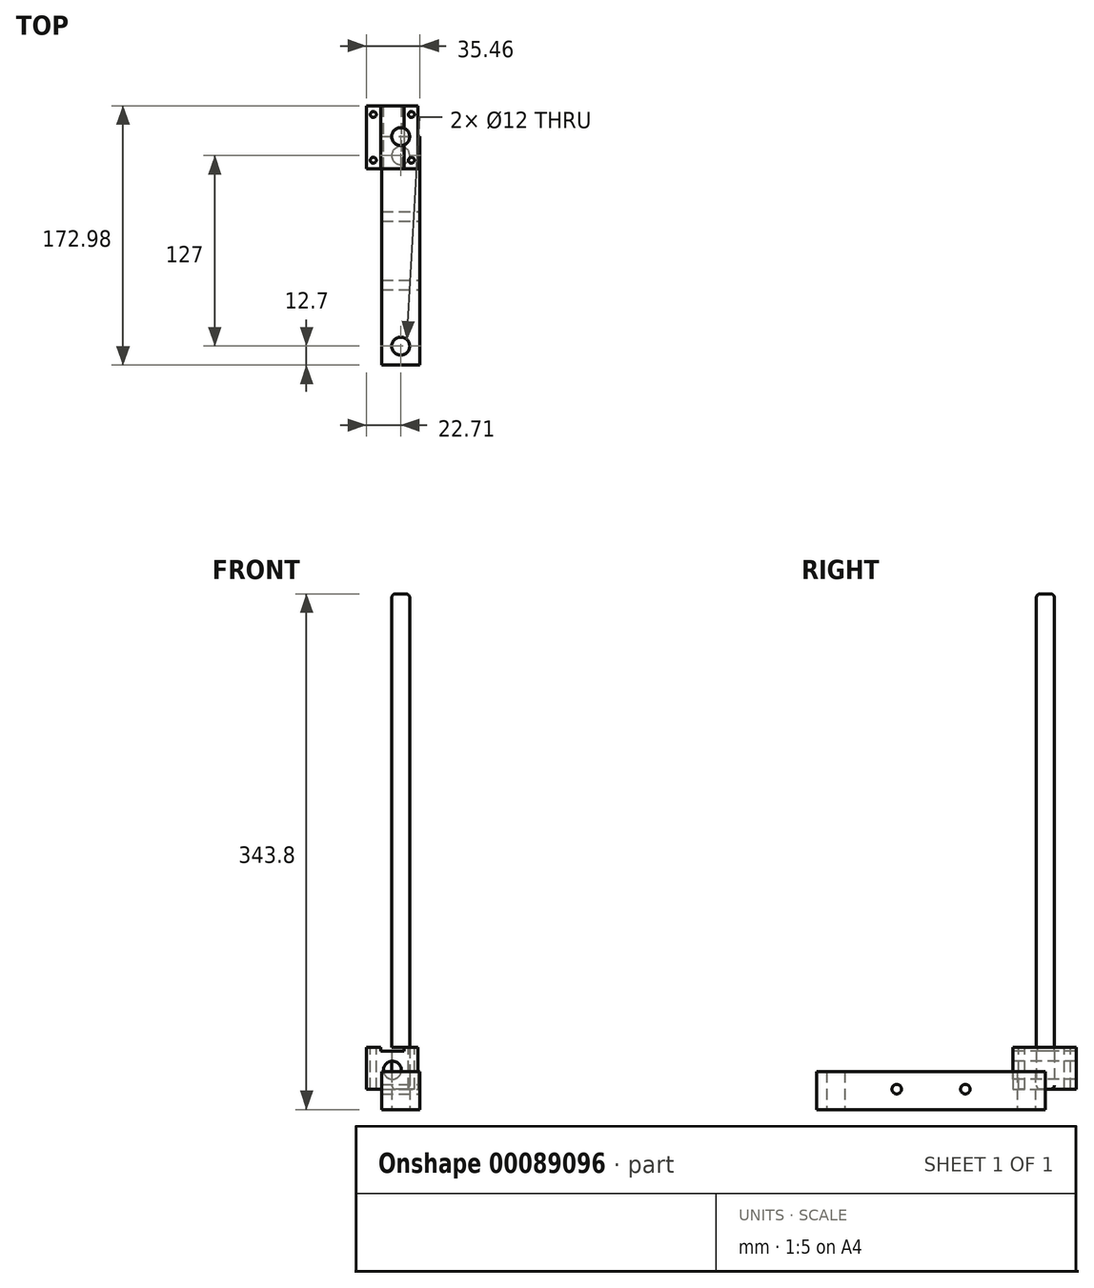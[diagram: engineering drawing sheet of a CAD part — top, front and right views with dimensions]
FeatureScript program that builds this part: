
annotation { "Feature Type Name" : "Feature", "Feature Type Description" : "" }
export const myFeature = defineFeature(function(context is Context, id is Id, definition is map)
    precondition{}
    {
        {
            var Q0;
            Q0=qCreatedBy(makeId("Top.planeOp"),FACE);
            var sketch = newSketch(context, id + "F0", { "sketchPlane" : qUnion([Q0])});
            skCircle(sketch, "E0", {"center": v(0, 0) * mm, "radius": 6 * mm});
            skSolve(sketch);
        }
        {
            var Q0;
            Q0 = qSketchRegion(id + "F0", true);
            extrude(context, id + "F1", {"entities" : qUnion([Q0]), "depth" : 330.2 * mm});
        }
        {
            var Q0;
            Q0=makeQuery(id+"F1.opExtrude","CAP_EDGE",EDGE,{"disambiguationData":[OSD([sQuery(id+"F0.wireOp",EDGE,"E0")])],"isStart":false});
            var Q1;
            Q1=makeQuery(id+"F1.opExtrude","CAP_EDGE",EDGE,{"disambiguationData":[OSD([sQuery(id+"F0.wireOp",EDGE,"E0")])],"isStart":true});
            fillet(context, id + "F2", {"entities" : qUnion([Q0, Q1]), "radius" : 2.54 * mm, "tangentPropagation" : true, "allowEdgeOverflow" : false});
        }
        {
            var Q0;
            Q0=qCreatedBy(makeId("Front.planeOp"),FACE);
            var sketch = newSketch(context, id + "F3", { "sketchPlane" : qUnion([Q0])});
            skLineSegment(sketch, "E1.bottom", {"start": v(-12.65, -13.6) * mm, "end": v(12.75, -13.6) * mm});
            skLineSegment(sketch, "E1.top", {"start": v(-12.65, 11.8) * mm, "end": v(12.75, 11.8) * mm});
            skLineSegment(sketch, "E1.left", {"start": v(-12.65, -13.6) * mm, "end": v(-12.65, 11.8) * mm});
            skLineSegment(sketch, "E1.right", {"start": v(12.75, -13.6) * mm, "end": v(12.75, 11.8) * mm});
            skSolve(sketch);
        }
        {
            var Q0;
            Q0 = qSketchRegion(id + "F3", true);
            extrude(context, id + "F4", {"entities" : qUnion([Q0]), "depth" : 152.4 * mm});
        }
        {
            var Q0;
            Q0=makeQuery(id+"F4.opExtrude","SWEPT_FACE",FACE,{"disambiguationData":[OSD([sQuery(id+"F3.wireOp",EDGE,"E1.bottom")])]});
            var sketch = newSketch(context, id + "F5", { "sketchPlane" : qUnion([Q0])});
            skPoint(sketch, "E2", {"position": v(0, 12.7) * mm});
            skPoint(sketch, "E3", {"position": v(0, 139.7) * mm});
            skSolve(sketch);
        }
        {
            var Q0;
            Q0=sQuery(id+"F5.wireOp",VERTEX,"E3");
            var Q1;
            Q1=sQuery(id+"F5.wireOp",VERTEX,"E2");
            var Q2;
            Q2=makeQuery(id+"F4.opExtrude","SWEPT_BODY",BODY,{"disambiguationData":[OSD([sQuery(id+"F3.wireOp",EDGE,"E1.bottom"),sQuery(id+"F3.wireOp",EDGE,"E1.top"),sQuery(id+"F3.wireOp",EDGE,"E1.left"),sQuery(id+"F3.wireOp",EDGE,"E1.right")])]});
            hole(context, id + "F6", {"style" : HoleStyle.SIMPLE, "endStyle" : HoleEndStyle.THROUGH, "holeDiameter" : 12 * mm, "locations" : qUnion([Q0, Q1]), "scope" : qUnion([Q2]), "isTappedThrough" : true});
        }
        {
            var Q0;
            Q0=makeQuery(id+"F4.opExtrude","SWEPT_FACE",FACE,{"disambiguationData":[OSD([sQuery(id+"F3.wireOp",EDGE,"E1.right")])]});
            var sketch = newSketch(context, id + "F7", { "sketchPlane" : qUnion([Q0])});
            skPoint(sketch, "E4", {"position": v(-53.34, 0) * mm});
            skPoint(sketch, "E5", {"position": v(-99.06, 0) * mm});
            skSolve(sketch);
        }
        {
            var Q0;
            Q0=sQuery(id+"F7.wireOp",VERTEX,"E5");
            var Q1;
            Q1=sQuery(id+"F7.wireOp",VERTEX,"E4");
            var Q2;
            Q2=makeQuery(id+"F4.opExtrude","SWEPT_BODY",BODY,{"disambiguationData":[OSD([sQuery(id+"F3.wireOp",EDGE,"E1.bottom"),sQuery(id+"F3.wireOp",EDGE,"E1.top"),sQuery(id+"F3.wireOp",EDGE,"E1.left"),sQuery(id+"F3.wireOp",EDGE,"E1.right")])]});
            hole(context, id + "F8", {"style" : HoleStyle.SIMPLE, "endStyle" : HoleEndStyle.THROUGH, "holeDiameter" : 6.35 * mm, "locations" : qUnion([Q0, Q1]), "scope" : qUnion([Q2]), "isTappedThrough" : true});
        }
        {
            var Q0;
            Q0=qCreatedBy(makeId("Top.planeOp"),FACE);
            var sketch = newSketch(context, id + "F9", { "sketchPlane" : qUnion([Q0])});
            skLineSegment(sketch, "E6.bottom", {"start": v(-22.71, -21.58) * mm, "end": v(11.58, -21.58) * mm});
            skLineSegment(sketch, "E6.top", {"start": v(-22.71, 20.58) * mm, "end": v(11.58, 20.58) * mm});
            skLineSegment(sketch, "E6.left", {"start": v(-22.71, -21.58) * mm, "end": v(-22.71, 20.58) * mm});
            skLineSegment(sketch, "E6.right", {"start": v(11.58, -21.58) * mm, "end": v(11.58, 20.58) * mm});
            skSolve(sketch);
        }
        {
            var Q0;
            Q0=makeQuery(id+"F9.imprint","IMPRINT",FACE,{"disambiguationData":[TD([[makeQuery(id+"F9.imprint","IMPRINT",EDGE,{"derivedFrom":sQuery(id+"F9.wireOp",EDGE,"E6.bottom")}),1.0]])]});
            extrude(context, id + "F10", {"entities" : qUnion([Q0]), "depth" : 27.94 * mm});
        }
        {
            var Q0;
            Q0=makeQuery(id+"F10.opExtrude","CAP_FACE",FACE,{"disambiguationData":[OSD([sQuery(id+"F9.wireOp",EDGE,"E6.bottom"),sQuery(id+"F9.wireOp",EDGE,"E6.top"),sQuery(id+"F9.wireOp",EDGE,"E6.left"),sQuery(id+"F9.wireOp",EDGE,"E6.right")])],"isStart":false});
            var sketch = newSketch(context, id + "F11", { "sketchPlane" : qUnion([Q0])});
            skPoint(sketch, "E7", {"position": v(-18.27, -15.74) * mm});
            skPoint(sketch, "E8", {"position": v(-18.27, 14.74) * mm});
            skLineSegment(sketch, "E9", {"start": v(-5.57, 20.58) * mm, "end": v(-5.57, -21.58) * mm});
            skPoint(sketch, "E10.MirrorP", {"position": v(7.13, 14.74) * mm});
            skPoint(sketch, "E11.MirrorP", {"position": v(7.13, -15.74) * mm});
            skSolve(sketch);
        }
        {
            var Q0;
            Q0=sQuery(id+"F11.wireOp",VERTEX,"E8");
            var Q1;
            Q1=sQuery(id+"F11.wireOp",VERTEX,"E7");
            var Q2;
            Q2=sQuery(id+"F11.wireOp",VERTEX,"E11.MirrorP");
            var Q3;
            Q3=sQuery(id+"F11.wireOp",VERTEX,"E10.MirrorP");
            var Q4;
            Q4=makeQuery(id+"F10.opExtrude","SWEPT_BODY",BODY,{"disambiguationData":[OSD([sQuery(id+"F9.wireOp",EDGE,"E6.bottom"),sQuery(id+"F9.wireOp",EDGE,"E6.top"),sQuery(id+"F9.wireOp",EDGE,"E6.left"),sQuery(id+"F9.wireOp",EDGE,"E6.right")])]});
            hole(context, id + "F12", {"style" : HoleStyle.SIMPLE, "endStyle" : HoleEndStyle.THROUGH, "holeDiameter" : 4 * mm, "locations" : qUnion([Q0, Q1, Q2, Q3]), "scope" : qUnion([Q4]), "isTappedThrough" : true});
        }
        {
            var Q0;
            Q0=makeQuery(id+"F10.opExtrude","SWEPT_FACE",FACE,{"disambiguationData":[OSD([sQuery(id+"F9.wireOp",EDGE,"E6.bottom")])]});
            var sketch = newSketch(context, id + "F13", { "sketchPlane" : qUnion([Q0])});
            skPoint(sketch, "E12", {"position": v(-5.57, 13.97) * mm});
            skPoint(sketch, "E13", {"position": v(-5.57, 12.6) * mm});
            skLineSegment(sketch, "E14.bottom", {"start": v(-5.57, 27.94) * mm, "end": v(-13.43, 27.94) * mm});
            skLineSegment(sketch, "E14.top", {"start": v(-5.57, 25.26) * mm, "end": v(-13.43, 25.26) * mm});
            skLineSegment(sketch, "E14.right", {"start": v(-13.43, 27.94) * mm, "end": v(-13.43, 25.26) * mm});
            skLineSegment(sketch, "E15.MirrorCS", {"start": v(-5.57, 25.26) * mm, "end": v(2.3, 25.26) * mm});
            skLineSegment(sketch, "E16.MirrorCS", {"start": v(2.3, 27.94) * mm, "end": v(2.3, 25.26) * mm});
            skLineSegment(sketch, "E17.MirrorCS", {"start": v(-5.57, 27.94) * mm, "end": v(2.3, 27.94) * mm});
            skSolve(sketch);
        }
        {
            var Q0;
            Q0=sQuery(id+"F13.wireOp",VERTEX,"E13");
            var Q1;
            Q1=makeQuery(id+"F10.opExtrude","SWEPT_BODY",BODY,{"disambiguationData":[OSD([sQuery(id+"F9.wireOp",EDGE,"E6.bottom"),sQuery(id+"F9.wireOp",EDGE,"E6.top"),sQuery(id+"F9.wireOp",EDGE,"E6.left"),sQuery(id+"F9.wireOp",EDGE,"E6.right")])]});
            hole(context, id + "F14", {"style" : HoleStyle.SIMPLE, "endStyle" : HoleEndStyle.THROUGH, "holeDiameter" : 12 * mm, "locations" : qUnion([Q0]), "scope" : qUnion([Q1]), "isTappedThrough" : true});
        }
        {
            var Q0;
            Q0=makeQuery(id+"F13.imprint","IMPRINT",FACE,{"disambiguationData":[TD([[makeQuery(id+"F13.imprint","IMPRINT",EDGE,{"derivedFrom":sQuery(id+"F13.wireOp",EDGE,"E14.bottom")}),-1.0]])]});
            var Q1;
            Q1=makeQuery(id+"F10.opExtrude","SWEPT_FACE",FACE,{"disambiguationData":[OSD([sQuery(id+"F9.wireOp",EDGE,"E6.top")])]});
            extrude(context, id + "F15", {"entities" : qUnion([Q0]), "operationType" : NewBodyOperationType.REMOVE, "endBound" : BoundingType.UP_TO_SURFACE, "oppositeDirection" : true, "endBoundEntityFace" : qUnion([Q1]), "depth" : 25.4 * mm});
        }
    });
